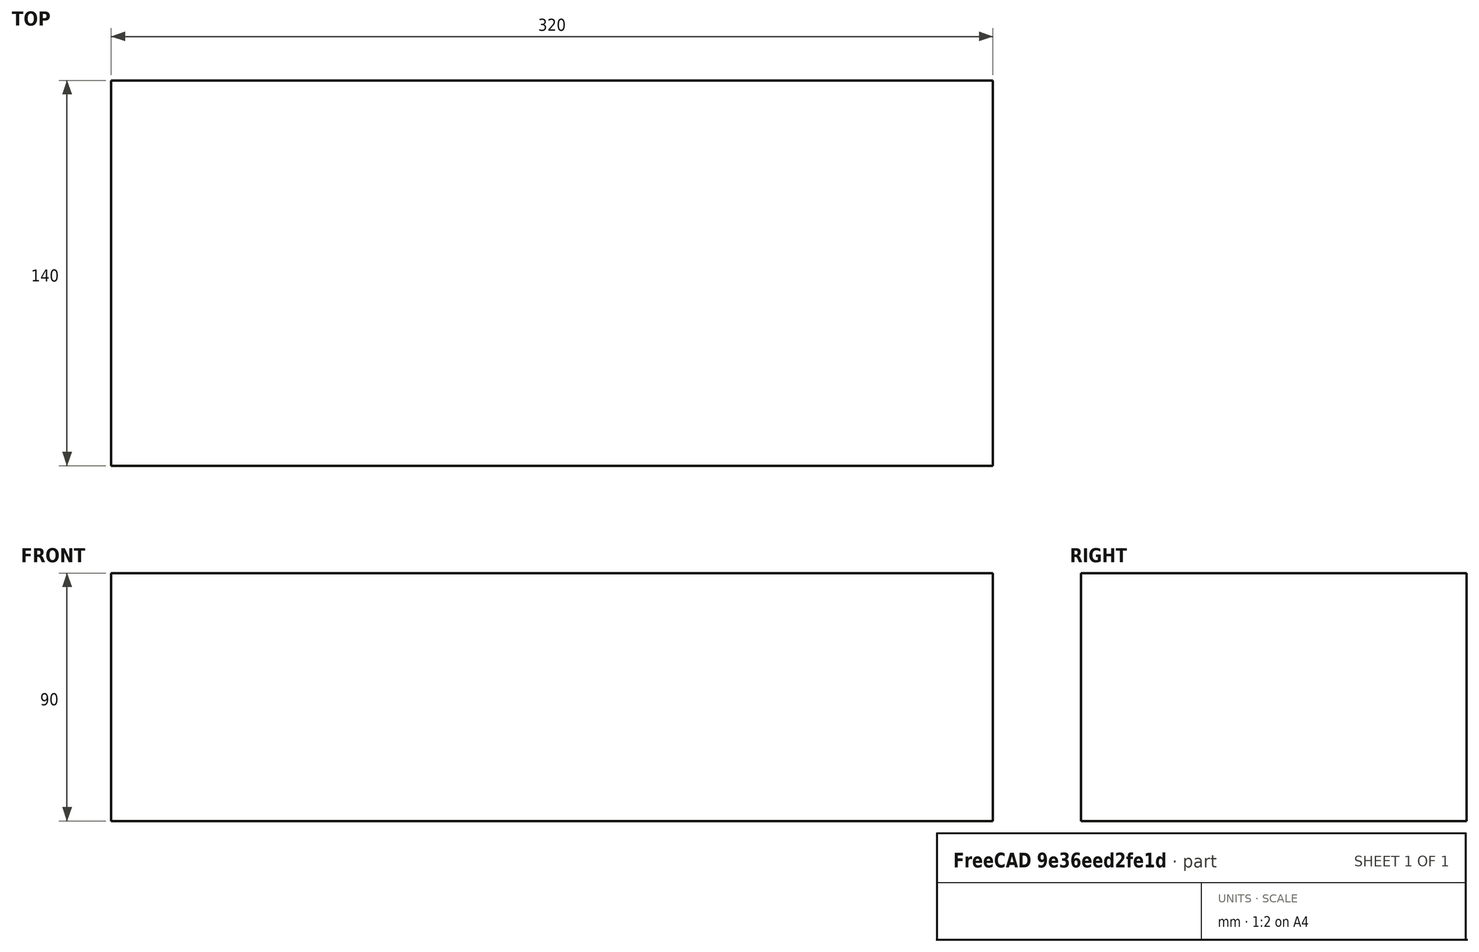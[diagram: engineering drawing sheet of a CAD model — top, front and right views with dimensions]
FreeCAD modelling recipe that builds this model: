
FCSTD DOCUMENT  (FreeCAD 1.0R39109 (Git))
Label: 028_table_clamp
License: All rights reserved
LicenseURL: http://en.wikipedia.org/wiki/All_rights_reserved
objects: Spreadsheet::Sheet×1, Sketcher::SketchObject×1, PartDesign::Pad×1, PartDesign::Body×1
note: 6 computed .brp shape members not serialized (recipe doc carries the construction recipe); baked Part::Feature solids carry a one-line shape summary decoded from their .brp

FEATURE [Spreadsheet::Sheet] Spreadsheet
  cells = A4='length; B4(length)=500; A5='width; B5(width)=140; A6='height; B6(height)=90
FEATURE [Sketcher::SketchObject] Sketch
  ArcFitTolerance = 1e-06
  AttachmentSupport = -> [XY_Plane]
  FullyConstrained = true
  MakeInternals = false
  MapMode = 5
  expr: Constraints[11] = Spreadsheet.length - 2 * Spreadsheet.height
  expr: Constraints[12] = Spreadsheet.width
  sketch-geometry (5):
    g0: LineSegment StartX=-160 StartY=70 StartZ=0 EndX=-160 EndY=-70 EndZ=0
    g1: LineSegment StartX=-160 StartY=-70 StartZ=0 EndX=160 EndY=-70 EndZ=0
    g2: LineSegment StartX=160 StartY=-70 StartZ=0 EndX=160 EndY=70 EndZ=0
    g3: LineSegment StartX=160 StartY=70 StartZ=0 EndX=-160 EndY=70 EndZ=0
    g4: LineSegment [constr] StartX=-160 StartY=70 StartZ=0 EndX=160 EndY=-70 EndZ=0
  constraints (13):
    c: Coincident(g0,g1)
    c: Coincident(g1,g2)
    c: Coincident(g2,g3)
    c: Coincident(g3,g0)
    c: Vertical(g0)
    c: Vertical(g2)
    c: Horizontal(g1)
    c: Horizontal(g3)
    c: Coincident(g4,g0)
    c: Coincident(g4,g1)
    c: Symmetric(g4,g4,g-1)
    c: DistanceX(g3,g3) = 320
    c: DistanceY(g0,g0) = 140
FEATURE [PartDesign::Pad] Pad
  Direction = (0,0,1)
  Length = 90
  Length2 = 10
  Midplane = true
  Profile = -> Sketch
  ReferenceAxis = -> Sketch [N_Axis]
  Suppressed = false
  Type = 0
  expr: Length = Spreadsheet.height
FEATURE [PartDesign::Body] Body
  AllowCompound = false
  Group = -> [Sketch,Pad]
  Origin = -> Origin
  Tip = -> Pad
